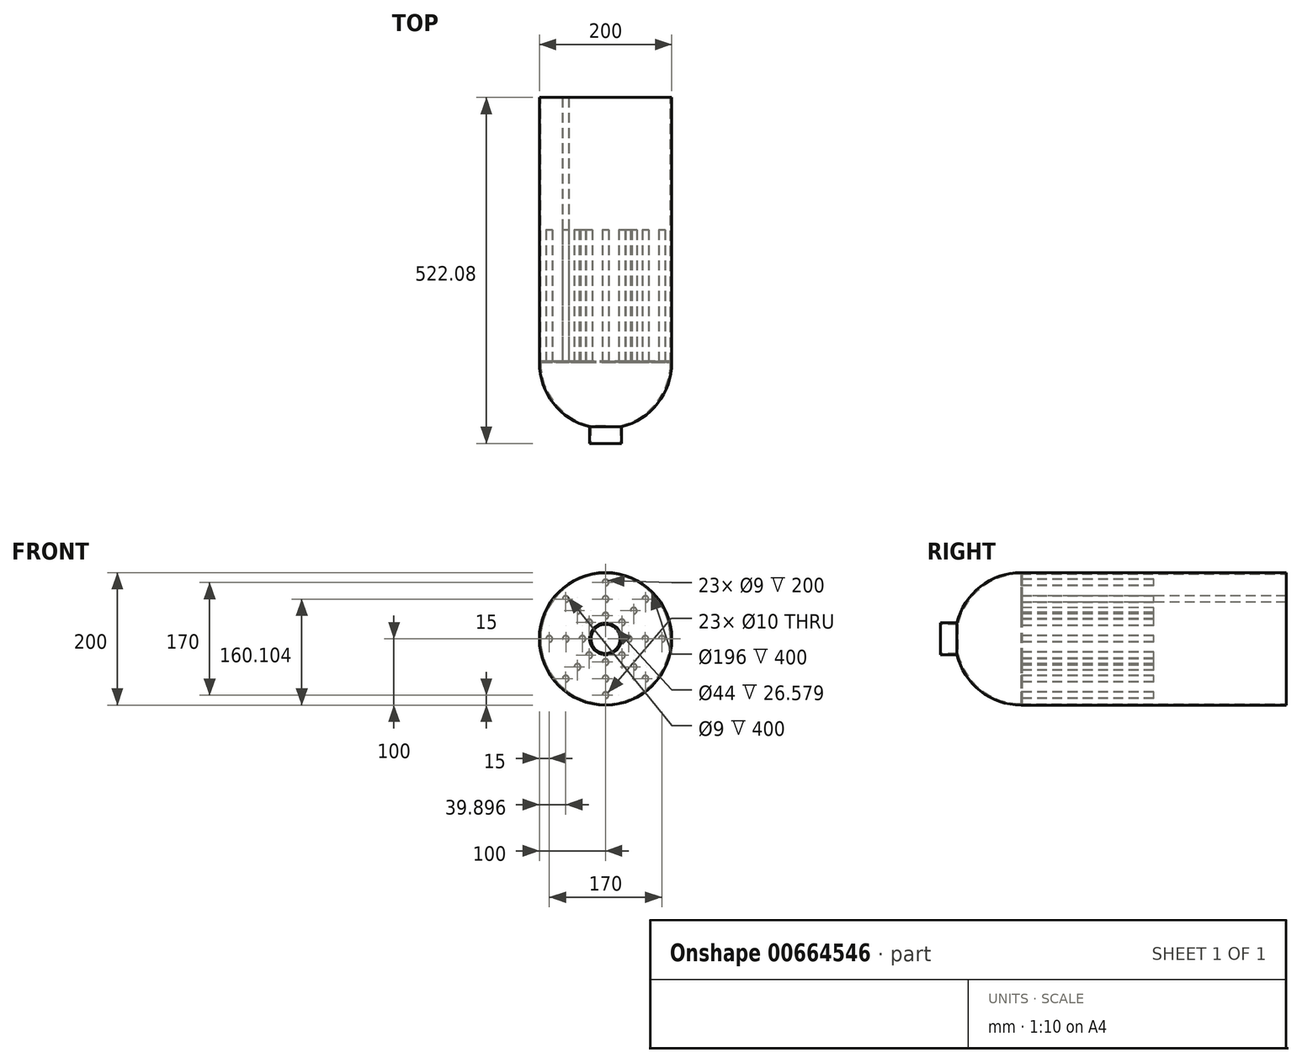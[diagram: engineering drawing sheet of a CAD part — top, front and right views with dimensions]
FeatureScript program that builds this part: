
annotation { "Feature Type Name" : "Feature", "Feature Type Description" : "" }
export const myFeature = defineFeature(function(context is Context, id is Id, definition is map)
    precondition{}
    {
        {
            var Q0;
            Q0=qCreatedBy(makeId("Front.planeOp"),FACE);
            var sketch = newSketch(context, id + "F0", { "sketchPlane" : qUnion([Q0])});
            skCircle(sketch, "E0", {"center": v(0, 0) * mm, "radius": 100 * mm});
            skCircle(sketch, "E1", {"center": v(0, 0) * mm, "radius": 98 * mm});
            skSolve(sketch);
        }
        {
            var Q0;
            Q0 = qSketchRegion(id + "F0", true);
            extrude(context, id + "F1", {"entities" : qUnion([Q0]), "depth" : 200 * mm, "offsetDistance" : 25 * mm, "hasSecondDirection" : true, "secondDirectionOppositeDirection" : true, "secondDirectionDepth" : 200 * mm});
        }
        {
            var Q0;
            Q0=qCreatedBy(makeId("Right.planeOp"),FACE);
            var sketch = newSketch(context, id + "F2", { "sketchPlane" : qUnion([Q0])});
            skArc(sketch, "E2", {"start": v(-200, 100) * mm, "mid": v(-300, 0) * mm, "end": v(-200, -100) * mm});
            skArc(sketch, "E3", {"start": v(-200, 98) * mm, "mid": v(-298, 0) * mm, "end": v(-200, -98) * mm});
            skLineSegment(sketch, "E4", {"start": v(-200, 100) * mm, "end": v(-200, 98) * mm});
            skLineSegment(sketch, "E5", {"start": v(-200, -98) * mm, "end": v(-200, -100) * mm});
            skLineSegment(sketch, "E6", {"start": v(-200, -100) * mm, "end": v(-200, 100) * mm, "construction": true});
            skSolve(sketch);
        }
        {
            var Q0;
            Q0 = qSketchRegion(id + "F2", true);
            var Q1;
            Q1=sQuery(id+"F2.wireOp",EDGE,"E6");
            revolve(context, id + "F3", {"operationType" : NewBodyOperationType.ADD, "entities" : qUnion([Q0]), "axis" : qUnion([Q1]), "revolveType" : RevolveType.SYMMETRIC, "angle" : 180 * degree});
        }
        {
            var Q0;
            Q0=qCreatedBy(makeId("Front.planeOp"),FACE);
            var sketch = newSketch(context, id + "F4", { "sketchPlane" : qUnion([Q0])});
            skCircle(sketch, "E7", {"center": v(0, 0) * mm, "radius": 24 * mm});
            skSolve(sketch);
        }
        {
            var Q0;
            Q0 = qSketchRegion(id + "F4", true);
            extrude(context, id + "F5", {"entities" : qUnion([Q0]), "operationType" : NewBodyOperationType.REMOVE, "endBound" : BoundingType.THROUGH_ALL, "depth" : 25 * mm, "offsetDistance" : 25 * mm});
        }
        {
            var Q0;
            Q0=qCreatedBy(makeId("Top.planeOp"),FACE);
            var sketch = newSketch(context, id + "F6", { "sketchPlane" : qUnion([Q0])});
            skLineSegment(sketch, "E8", {"start": v(5.28, 0) * mm, "end": v(5.28, -297.08) * mm, "construction": true});
            skPoint(sketch, "E9", {"position": v(5.28, -200) * mm});
            skSolve(sketch);
        }
        {
            var Q0;
            Q0=sQuery(id+"F6.wireOp",VERTEX,"E8.end");
            var Q1;
            Q1=qCreatedBy(makeId("Front.planeOp"),FACE);
            cPlane(context, id + "F7", {"entities" : qUnion([Q0, Q1]), "cplaneType" : CPlaneType.PLANE_POINT, "offset" : 25 * mm, "width" : 150 * mm, "height" : 150 * mm});
        }
        {
            var Q0;
            Q0=qCreatedBy(id+"F7.planeOp",FACE);
            var sketch = newSketch(context, id + "F8", { "sketchPlane" : qUnion([Q0])});
            skCircle(sketch, "E10", {"center": v(0, 0) * mm, "radius": 24 * mm});
            skCircle(sketch, "E11", {"center": v(0, 0) * mm, "radius": 22 * mm});
            skSolve(sketch);
        }
        {
            var Q0;
            Q0 = qSketchRegion(id + "F8", true);
            var Q1;
            Q1=makeQuery(id+"F3.opRevolve","SWEPT_FACE",FACE,{"disambiguationData":[OSD([sQuery(id+"F2.wireOp",EDGE,"E3")])]});
            var Q2;
            Q2=makeQuery(id+"F1.opExtrude","SWEPT_BODY",BODY,{"disambiguationData":[OSD([sQuery(id+"F0.wireOp",EDGE,"E0"),sQuery(id+"F0.wireOp",EDGE,"E1")])]});
            var Q3;
            Q3=makeQuery(id+"F1.opExtrude","SWEPT_BODY",BODY,{"disambiguationData":[OSD([sQuery(id+"F0.wireOp",EDGE,"E0"),sQuery(id+"F0.wireOp",EDGE,"E1")])]});
            extrude(context, id + "F9", {"entities" : qUnion([Q0]), "operationType" : NewBodyOperationType.ADD, "endBound" : BoundingType.UP_TO_SURFACE, "oppositeDirection" : true, "depth" : 30 * mm, "endBoundEntityFace" : qUnion([Q1]), "endBoundEntityBody" : qUnion([Q2]), "offsetDistance" : 25 * mm, "hasSecondDirection" : true, "secondDirectionOppositeDirection" : false, "secondDirectionDepth" : 25 * mm, "secondDirectionBoundEntityBody" : qUnion([Q3])});
        }
        {
            var Q0;
            Q0=sQuery(id+"F6.wireOp",VERTEX,"E9");
            var Q1;
            Q1=qCreatedBy(makeId("Front.planeOp"),FACE);
            cPlane(context, id + "F10", {"entities" : qUnion([Q0, Q1]), "cplaneType" : CPlaneType.PLANE_POINT, "offset" : 25 * mm, "width" : 150 * mm, "height" : 150 * mm});
        }
        {
            var Q0;
            Q0=qCreatedBy(id+"F10.planeOp",FACE);
            var sketch = newSketch(context, id + "F11", { "sketchPlane" : qUnion([Q0])});
            skCircle(sketch, "E12", {"center": v(-35, 0) * mm, "radius": 5 * mm});
            skCircle(sketch, "E13", {"center": v(-35, 0) * mm, "radius": 4.5 * mm});
            skCircle(sketch, "E14.1.0.0", {"center": v(-60, 0) * mm, "radius": 4.5 * mm});
            skCircle(sketch, "E14.1.0.1", {"center": v(-60, 0) * mm, "radius": 5 * mm});
            skCircle(sketch, "E14.2.0.0", {"center": v(-85, 0) * mm, "radius": 4.5 * mm});
            skCircle(sketch, "E14.2.0.1", {"center": v(-85, 0) * mm, "radius": 5 * mm});
            skLineSegment(sketch, "E14.direction1", {"start": v(-35, 0) * mm, "end": v(-60, 0) * mm, "construction": true});
            skCircle(sketch, "E15.1.0", {"center": v(-24.75, -24.75) * mm, "radius": 4.5 * mm});
            skCircle(sketch, "E15.1.1", {"center": v(-24.75, -24.75) * mm, "radius": 5 * mm});
            skCircle(sketch, "E15.1.2", {"center": v(-42.43, -42.43) * mm, "radius": 5 * mm});
            skCircle(sketch, "E15.1.3", {"center": v(-42.43, -42.43) * mm, "radius": 4.5 * mm});
            skCircle(sketch, "E15.1.4", {"center": v(-60.1, -60.1) * mm, "radius": 5 * mm});
            skCircle(sketch, "E15.1.5", {"center": v(-60.1, -60.1) * mm, "radius": 4.5 * mm});
            skCircle(sketch, "E15.2.0", {"center": v(0, -35) * mm, "radius": 4.5 * mm});
            skCircle(sketch, "E15.2.1", {"center": v(0, -35) * mm, "radius": 5 * mm});
            skCircle(sketch, "E15.2.2", {"center": v(0, -60) * mm, "radius": 5 * mm});
            skCircle(sketch, "E15.2.3", {"center": v(0, -60) * mm, "radius": 4.5 * mm});
            skCircle(sketch, "E15.2.4", {"center": v(0, -85) * mm, "radius": 5 * mm});
            skCircle(sketch, "E15.2.5", {"center": v(0, -85) * mm, "radius": 4.5 * mm});
            skCircle(sketch, "E15.3.0", {"center": v(24.75, -24.75) * mm, "radius": 4.5 * mm});
            skCircle(sketch, "E15.3.1", {"center": v(24.75, -24.75) * mm, "radius": 5 * mm});
            skCircle(sketch, "E15.3.2", {"center": v(42.43, -42.43) * mm, "radius": 5 * mm});
            skCircle(sketch, "E15.3.3", {"center": v(42.43, -42.43) * mm, "radius": 4.5 * mm});
            skCircle(sketch, "E15.3.4", {"center": v(60.1, -60.1) * mm, "radius": 5 * mm});
            skCircle(sketch, "E15.3.5", {"center": v(60.1, -60.1) * mm, "radius": 4.5 * mm});
            skCircle(sketch, "E15.4.0", {"center": v(35, 0) * mm, "radius": 4.5 * mm});
            skCircle(sketch, "E15.4.1", {"center": v(35, 0) * mm, "radius": 5 * mm});
            skCircle(sketch, "E15.4.2", {"center": v(60, 0) * mm, "radius": 5 * mm});
            skCircle(sketch, "E15.4.3", {"center": v(60, 0) * mm, "radius": 4.5 * mm});
            skCircle(sketch, "E15.4.4", {"center": v(85, 0) * mm, "radius": 5 * mm});
            skCircle(sketch, "E15.4.5", {"center": v(85, 0) * mm, "radius": 4.5 * mm});
            skCircle(sketch, "E15.5.0", {"center": v(24.75, 24.75) * mm, "radius": 4.5 * mm});
            skCircle(sketch, "E15.5.1", {"center": v(24.75, 24.75) * mm, "radius": 5 * mm});
            skCircle(sketch, "E15.5.2", {"center": v(42.43, 42.43) * mm, "radius": 5 * mm});
            skCircle(sketch, "E15.5.3", {"center": v(42.43, 42.43) * mm, "radius": 4.5 * mm});
            skCircle(sketch, "E15.5.4", {"center": v(60.1, 60.1) * mm, "radius": 5 * mm});
            skCircle(sketch, "E15.5.5", {"center": v(60.1, 60.1) * mm, "radius": 4.5 * mm});
            skCircle(sketch, "E15.6.0", {"center": v(0, 35) * mm, "radius": 4.5 * mm});
            skCircle(sketch, "E15.6.1", {"center": v(0, 35) * mm, "radius": 5 * mm});
            skCircle(sketch, "E15.6.2", {"center": v(0, 60) * mm, "radius": 5 * mm});
            skCircle(sketch, "E15.6.3", {"center": v(0, 60) * mm, "radius": 4.5 * mm});
            skCircle(sketch, "E15.6.4", {"center": v(0, 85) * mm, "radius": 5 * mm});
            skCircle(sketch, "E15.6.5", {"center": v(0, 85) * mm, "radius": 4.5 * mm});
            skPoint(sketch, "E15.center", {"position": v(0, 0) * mm});
            skCircle(sketch, "E16.0.7.0", {"center": v(-24.75, 24.75) * mm, "radius": 4.5 * mm});
            skCircle(sketch, "E16.2.7.0", {"center": v(-24.75, 24.75) * mm, "radius": 5 * mm});
            skCircle(sketch, "E16.4.7.0", {"center": v(-42.43, 42.43) * mm, "radius": 5 * mm});
            skCircle(sketch, "E16.6.7.0", {"center": v(-42.43, 42.43) * mm, "radius": 4.5 * mm});
            skCircle(sketch, "E16.8.7.0", {"center": v(-60.1, 60.1) * mm, "radius": 5 * mm});
            skCircle(sketch, "E16.10.7.0", {"center": v(-60.1, 60.1) * mm, "radius": 4.5 * mm});
            skSolve(sketch);
        }
        {
            var Q0;
            Q0 = qSketchRegion(id + "F11", true);
            var Q1;
            Q1=qCreatedBy(makeId("Front.planeOp"),FACE);
            extrude(context, id + "F12", {"entities" : qUnion([Q0]), "endBound" : BoundingType.UP_TO_SURFACE, "oppositeDirection" : true, "depth" : 25 * mm, "endBoundEntityFace" : qUnion([Q1]), "offsetDistance" : 25 * mm});
        }
        {
            var Q0;
            Q0=qCreatedBy(id+"F10.planeOp",FACE);
            var sketch = newSketch(context, id + "F13", { "sketchPlane" : qUnion([Q0])});
            skCircle(sketch, "E17", {"center": v(0, 0) * mm, "radius": 98 * mm});
            skCircle(sketch, "E18.0", {"center": v(60.1, -60.1) * mm, "radius": 5 * mm});
            skCircle(sketch, "E18.1", {"center": v(42.43, -42.43) * mm, "radius": 5 * mm});
            skCircle(sketch, "E18.2", {"center": v(24.75, -24.75) * mm, "radius": 5 * mm});
            skCircle(sketch, "E18.3", {"center": v(0, -35) * mm, "radius": 5 * mm});
            skCircle(sketch, "E18.4", {"center": v(0, -60) * mm, "radius": 5 * mm});
            skCircle(sketch, "E18.5", {"center": v(0, -85) * mm, "radius": 5 * mm});
            skCircle(sketch, "E18.6", {"center": v(-24.75, -24.75) * mm, "radius": 5 * mm});
            skCircle(sketch, "E18.7", {"center": v(-42.43, -42.43) * mm, "radius": 5 * mm});
            skCircle(sketch, "E18.8", {"center": v(-60.1, -60.1) * mm, "radius": 5 * mm});
            skCircle(sketch, "E18.9", {"center": v(-35, 0) * mm, "radius": 5 * mm});
            skCircle(sketch, "E18.10", {"center": v(-60, 0) * mm, "radius": 5 * mm});
            skCircle(sketch, "E18.11", {"center": v(-85, 0) * mm, "radius": 5 * mm});
            skCircle(sketch, "E18.12", {"center": v(35, 0) * mm, "radius": 5 * mm});
            skCircle(sketch, "E18.13", {"center": v(60, 0) * mm, "radius": 5 * mm});
            skCircle(sketch, "E18.14", {"center": v(85, 0) * mm, "radius": 5 * mm});
            skCircle(sketch, "E18.15", {"center": v(24.75, 24.75) * mm, "radius": 5 * mm});
            skCircle(sketch, "E18.16", {"center": v(42.43, 42.43) * mm, "radius": 5 * mm});
            skCircle(sketch, "E18.17", {"center": v(60.1, 60.1) * mm, "radius": 5 * mm});
            skCircle(sketch, "E18.18", {"center": v(0, 35) * mm, "radius": 5 * mm});
            skCircle(sketch, "E18.19", {"center": v(0, 60) * mm, "radius": 5 * mm});
            skCircle(sketch, "E18.20", {"center": v(0, 85) * mm, "radius": 5 * mm});
            skCircle(sketch, "E18.21", {"center": v(-60.1, 60.1) * mm, "radius": 5 * mm});
            skCircle(sketch, "E18.22", {"center": v(-42.43, 42.43) * mm, "radius": 5 * mm});
            skCircle(sketch, "E18.23", {"center": v(-24.75, 24.75) * mm, "radius": 5 * mm});
            skSolve(sketch);
        }
        {
            var Q0;
            Q0 = qSketchRegion(id + "F13", true);
            extrude(context, id + "F14", {"entities" : qUnion([Q0]), "oppositeDirection" : true, "depth" : 2 * mm, "offsetDistance" : 25 * mm});
        }
        {
            var Q0;
            Q0=makeQuery(id+"F12.opExtrude","SWEPT_BODY",BODY,{"disambiguationData":[OSD([sQuery(id+"F11.wireOp",EDGE,"E16.8.7.0"),sQuery(id+"F11.wireOp",EDGE,"E16.10.7.0")])]});
            var Q1;
            Q1=qCreatedBy(makeId("Front.planeOp"),FACE);
            mirror(context, id + "F15", {"operationType" : NewBodyOperationType.ADD, "entities" : qUnion([Q0]), "mirrorPlane" : qUnion([Q1])});
        }
    });
